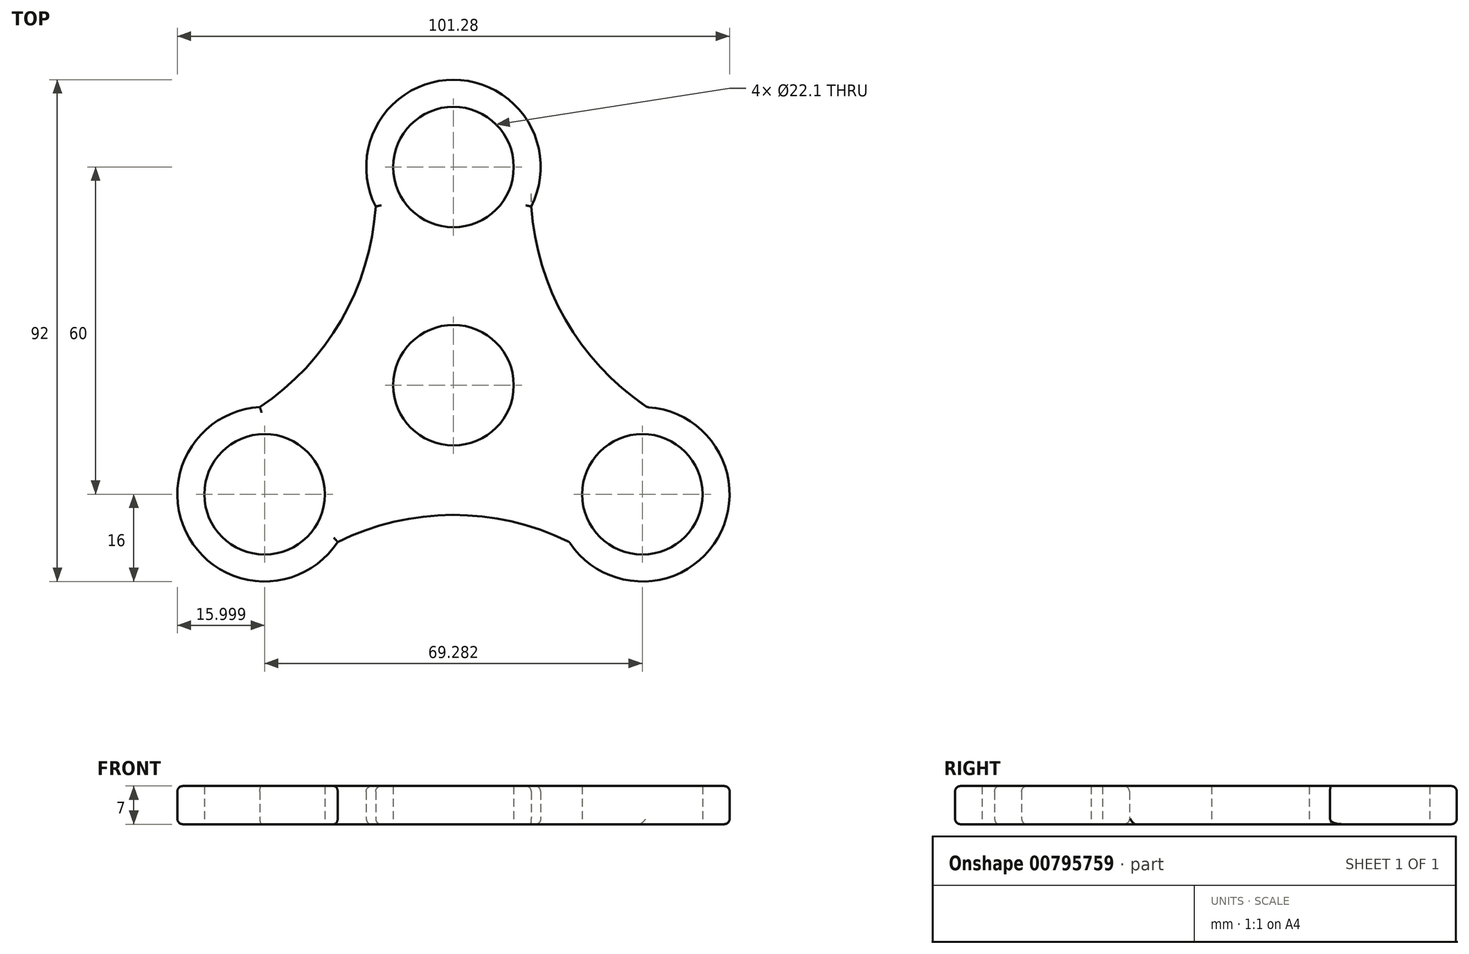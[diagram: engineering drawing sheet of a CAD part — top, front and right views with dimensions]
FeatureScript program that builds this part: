
annotation { "Feature Type Name" : "Feature", "Feature Type Description" : "" }
export const myFeature = defineFeature(function(context is Context, id is Id, definition is map)
    precondition{}
    {
        {
            var Q0;
            Q0=qCreatedBy(makeId("Top.planeOp"),FACE);
            var sketch = newSketch(context, id + "F0", { "sketchPlane" : qUnion([Q0])});
            skCircle(sketch, "E0", {"center": v(0, 0) * mm, "radius": 11.05 * mm});
            skCircle(sketch, "E1", {"center": v(0, 40) * mm, "radius": 11.05 * mm});
            skCircle(sketch, "E2.1.0", {"center": v(34.64, -20) * mm, "radius": 11.05 * mm});
            skCircle(sketch, "E2.2.0", {"center": v(-34.64, -20) * mm, "radius": 11.05 * mm});
            skLineSegment(sketch, "E2.anchor1", {"start": v(0, 0) * mm, "end": v(0, 40) * mm, "construction": true});
            skLineSegment(sketch, "E2.anchor2", {"start": v(0, 0) * mm, "end": v(-34.64, -20) * mm, "construction": true});
            skCircle(sketch, "E3", {"center": v(0, 40) * mm, "radius": 16 * mm});
            skCircle(sketch, "E4.1.0", {"center": v(-34.64, -20) * mm, "radius": 16 * mm});
            skCircle(sketch, "E4.2.0", {"center": v(34.64, -20) * mm, "radius": 16 * mm});
            skLineSegment(sketch, "E5", {"start": v(0, 40) * mm, "end": v(34.64, -20) * mm, "construction": true});
            skLineSegment(sketch, "E6", {"start": v(10.3, 39.65) * mm, "end": v(41.2, -13.87) * mm, "construction": true});
            skArc(sketch, "E7", {"start": v(14.27, 32.77) * mm, "mid": v(20.6, 11.9) * mm, "end": v(35.51, -4.02) * mm});
            skArc(sketch, "E8.1.0", {"start": v(-35.51, -4.02) * mm, "mid": v(-20.6, 11.9) * mm, "end": v(-14.27, 32.77) * mm});
            skArc(sketch, "E8.2.0", {"start": v(21.24, -28.74) * mm, "mid": v(0, -23.79) * mm, "end": v(-21.24, -28.74) * mm});
            skSolve(sketch);
        }
        {
            var Q0;
            Q0=makeQuery(id+"F0.imprint","IMPRINT",FACE,{"disambiguationData":[TD([[makeQuery(id+"F0.imprint","IMPRINT",EDGE,{"derivedFrom":sQuery(id+"F0.wireOp",EDGE,"E2.2.0")}),-1.0]])]});
            var Q1;
            Q1=makeQuery(id+"F0.imprint","IMPRINT",FACE,{"disambiguationData":[TD([[makeQuery(id+"F0.imprint","IMPRINT",EDGE,{"derivedFrom":sQuery(id+"F0.wireOp",EDGE,"E1")}),-1.0]])]});
            var Q2;
            Q2=makeQuery(id+"F0.imprint","IMPRINT",FACE,{"disambiguationData":[TD([[makeQuery(id+"F0.imprint","IMPRINT",EDGE,{"derivedFrom":sQuery(id+"F0.wireOp",EDGE,"E2.1.0")}),-1.0]])]});
            var Q3;
            Q3=makeQuery(id+"F0.imprint","IMPRINT",FACE,{"disambiguationData":[TD([[makeQuery(id+"F0.imprint","IMPRINT",EDGE,{"derivedFrom":sQuery(id+"F0.wireOp",EDGE,"E0")}),-1.0]])]});
            extrude(context, id + "F1", {"entities" : qUnion([Q0, Q1, Q2, Q3]), "depth" : 7 * mm, "offsetDistance" : 25 * mm});
        }
        {
            var Q0;
            Q0=makeQuery(id+"F1.opExtrude","CAP_EDGE",EDGE,{"disambiguationData":[OSD([sQuery(id+"F0.wireOp",EDGE,"E4.1.0")])],"isStart":false});
            var Q1;
            Q1=makeQuery(id+"F1.opExtrude","CAP_EDGE",EDGE,{"disambiguationData":[OSD([sQuery(id+"F0.wireOp",EDGE,"E8.2.0")])],"isStart":false});
            var Q2;
            Q2=makeQuery(id+"F1.opExtrude","CAP_EDGE",EDGE,{"disambiguationData":[OSD([sQuery(id+"F0.wireOp",EDGE,"E4.2.0")])],"isStart":false});
            var Q3;
            Q3=makeQuery(id+"F1.opExtrude","CAP_EDGE",EDGE,{"disambiguationData":[OSD([sQuery(id+"F0.wireOp",EDGE,"E7")])],"isStart":false});
            var Q4;
            Q4=makeQuery(id+"F1.opExtrude","CAP_EDGE",EDGE,{"disambiguationData":[OSD([sQuery(id+"F0.wireOp",EDGE,"E3")])],"isStart":false});
            var Q5;
            Q5=makeQuery(id+"F1.opExtrude","CAP_EDGE",EDGE,{"disambiguationData":[OSD([sQuery(id+"F0.wireOp",EDGE,"E8.1.0")])],"isStart":false});
            var Q6;
            Q6=makeQuery(id+"F1.opExtrude","CAP_EDGE",EDGE,{"disambiguationData":[OSD([sQuery(id+"F0.wireOp",EDGE,"E8.2.0")])],"isStart":true});
            var Q7;
            Q7=makeQuery(id+"F1.opExtrude","CAP_EDGE",EDGE,{"disambiguationData":[OSD([sQuery(id+"F0.wireOp",EDGE,"E4.1.0")])],"isStart":true});
            var Q8;
            Q8=makeQuery(id+"F1.opExtrude","SWEPT_FACE",FACE,{"disambiguationData":[OSD([sQuery(id+"F0.wireOp",EDGE,"E4.2.0")])]});
            var Q9;
            Q9=makeQuery(id+"F1.opExtrude","CAP_EDGE",EDGE,{"disambiguationData":[OSD([sQuery(id+"F0.wireOp",EDGE,"E8.1.0")])],"isStart":true});
            var Q10;
            Q10=makeQuery(id+"F1.opExtrude","CAP_EDGE",EDGE,{"disambiguationData":[OSD([sQuery(id+"F0.wireOp",EDGE,"E3")])],"isStart":true});
            fillet(context, id + "F2", {"entities" : qUnion([Q0, Q1, Q2, Q3, Q4, Q5, Q6, Q7, Q8, Q9, Q10]), "radius" : 1 * mm, "tangentPropagation" : true, "allowEdgeOverflow" : false});
        }
    });
